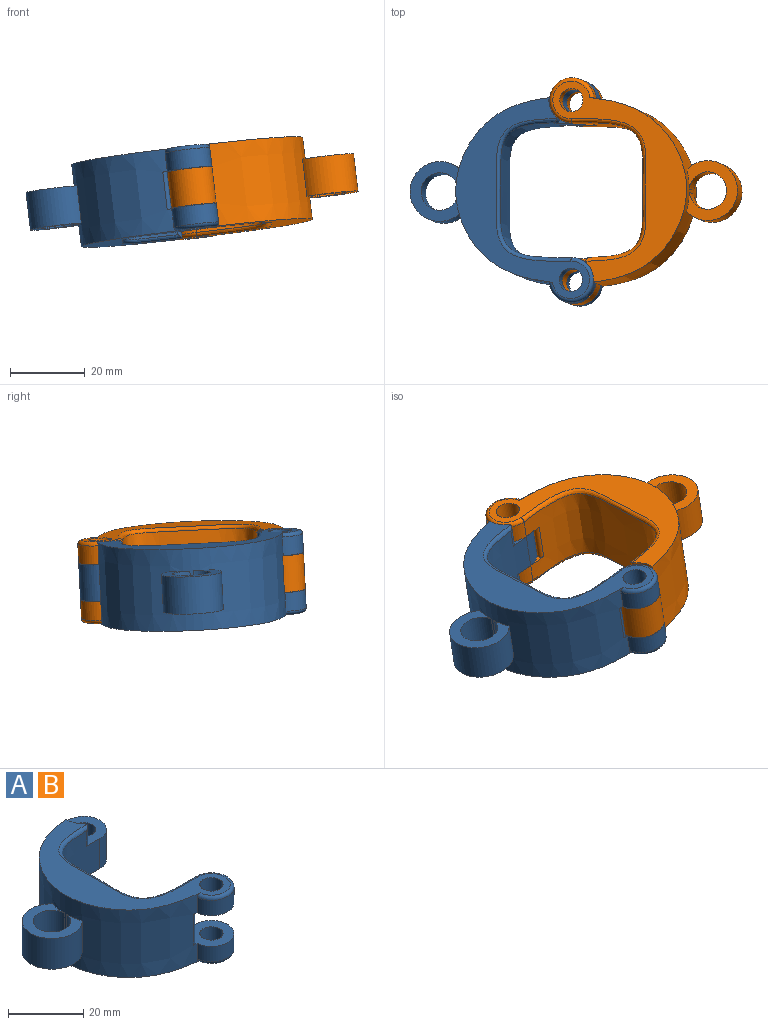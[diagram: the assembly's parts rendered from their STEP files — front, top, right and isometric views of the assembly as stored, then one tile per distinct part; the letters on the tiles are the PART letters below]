
ASSEMBLY  parts=2 mates=1
PART A: 29 faces, bbox 60.3x60.5x22 mm
  f0: extruded ~36.05x20mm, area 1225mm2, adj f3,f4,f7,f10,f12,f15,f16,f21
  f1: extruded ~49.28x26.04mm, area 1585.3mm2, adj f3,f4,f7,f8,f9,f10,f11,f12
  f2: cylinder r=3.1mm len=6.2mm, axis (0,0,-1), area 116.9mm2, adj f9,f15
  f3: cylinder r=6mm len=12mm, axis (0,0,-1), area 138.6mm2, adj f0,f1,f15,f23
  f4: cylinder r=6mm len=12mm, axis (0,0,-1), area 271.2mm2, adj f0,f1,f10,f12
  f5: cylinder r=3.1mm len=9.8mm, axis (0,0,-1), area 190.9mm2, adj f10,f12
  f6: cylinder r=3.1mm len=6.2mm, axis (0,0,-1), area 116.9mm2, adj f8,f16
  f7: cylinder r=6mm len=12mm, axis (0,0,-1), area 138.6mm2, adj f0,f1,f16,f26
  f8: plane 53.6x36.04mm, normal (0,0,1), area 525.1mm2, adj f1,f6,f11,f26,f27,f28
  f9: plane 53.6x36.04mm, normal (0,0,-1), area 525mm2, adj f1,f2,f13,f23,f24,f25
  f10: plane 12.05x12.01mm, normal (0,0,1), area 85.3mm2, adj f0,f1,f4,f5,f11,f28
  f11: cylinder r=6.05mm len=6.1mm, axis (0,0,1), area 32.6mm2, adj f1,f8,f10,f28
  f12: plane 12.05x12.01mm, normal (0,0,-1), area 85.3mm2, adj f0,f1,f4,f5,f13,f25
  f13: cylinder r=6.05mm len=6.1mm, axis (0,0,-1), area 32.6mm2, adj f1,f9,f12,f25
  f14: cylinder r=6.05mm len=10mm, axis (0,0,1), area 42.5mm2, adj f15,f16,f21,f22
  f15: plane 13.17x12.01mm, normal (0,0,1), area 85.5mm2, adj f0,f1,f2,f3,f14,f21,f22
  f16: plane 13.17x12.01mm, normal (0,0,-1), area 85.5mm2, adj f0,f1,f6,f7,f14,f21,f22
  f17: cylinder r=5mm len=10mm, axis (0,0,-1), area 305.9mm2, adj f1,f19,f20
  f18: cylinder r=8mm len=16mm, axis (0,0,-1), area 378.5mm2, adj f1,f19,f20
  f19: plane 16x13.76mm, normal (0,0,1), area 99.4mm2, adj f1,f17,f18
  f20: plane 16x13.76mm, normal (0,0,-1), area 99.4mm2, adj f1,f17,f18
  f21: cylinder r=1mm len=10mm, axis (0,0,-1), area 23.4mm2, adj f0,f14,f15,f16
  f22: cylinder r=1mm len=10mm, axis (0,0,-1), area 16.3mm2, adj f1,f14,f15,f16
  f23: torus R=5mm, axis (0,0,1), area 40.7mm2, adj f1,f3,f9,f24
  f24: bspline ~38.06x21.29mm, area 98.9mm2, adj f0,f9,f23,f25
  f25: cylinder r=1mm len=6.1mm, axis (0,0,-1), area 13.5mm2, adj f0,f9,f12,f13,f24
  f26: torus R=5mm, axis (0,0,1), area 40.7mm2, adj f1,f7,f8,f27
  f27: bspline ~38.06x36.48mm, area 98.9mm2, adj f0,f8,f26,f28
  f28: cylinder r=1mm len=6.1mm, axis (0,0,-1), area 13.5mm2, adj f0,f8,f10,f11,f27
PART B: same geometry as A
PLACE A rot(axis=(-0.38,-0.92,0),7.3deg) t=(24.41,-7.8,7.37)mm
PLACE B rot(axis=(0.06,-0.02,-1),180deg) t=(24.42,-7.8,7.37)mm
MATE revolute A.f5 <-> B.f14  axis (0.12,-0.05,-0.99) through (23.18,16.71,17.11)mm
